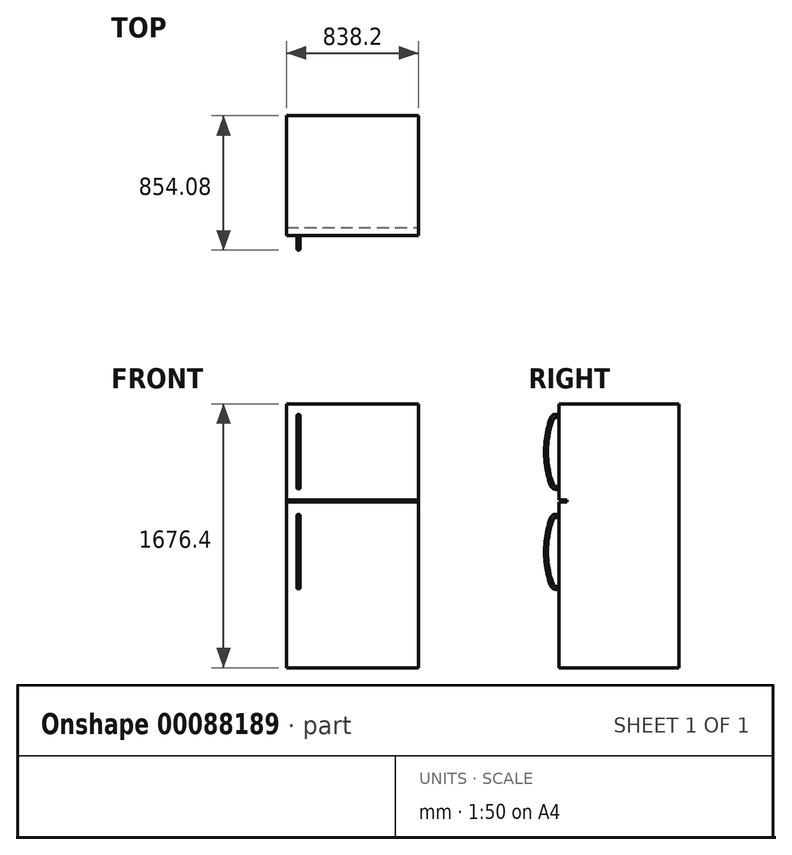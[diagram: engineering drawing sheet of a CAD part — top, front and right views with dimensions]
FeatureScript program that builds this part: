
annotation { "Feature Type Name" : "Feature", "Feature Type Description" : "" }
export const myFeature = defineFeature(function(context is Context, id is Id, definition is map)
    precondition{}
    {
        {
            var Q0;
            Q0=qCreatedBy(makeId("Front.planeOp"),FACE);
            var sketch = newSketch(context, id + "F0", { "sketchPlane" : qUnion([Q0])});
            skLineSegment(sketch, "E0.bottom", {"start": v(0, 0) * mm, "end": v(838.2, 0) * mm});
            skLineSegment(sketch, "E0.top", {"start": v(0, 1676.4) * mm, "end": v(838.2, 1676.4) * mm});
            skLineSegment(sketch, "E0.left", {"start": v(0, 0) * mm, "end": v(0, 1676.4) * mm});
            skLineSegment(sketch, "E0.right", {"start": v(838.2, 0) * mm, "end": v(838.2, 1676.4) * mm});
            skSolve(sketch);
        }
        {
            var Q0;
            Q0 = qSketchRegion(id + "F0", true);
            extrude(context, id + "F1", {"entities" : qUnion([Q0]), "depth" : 762 * mm});
        }
        {
            var Q0;
            Q0=makeQuery(id+"F1.opExtrude","CAP_FACE",FACE,{"disambiguationData":[OSD([sQuery(id+"F0.wireOp",EDGE,"E0.bottom"),sQuery(id+"F0.wireOp",EDGE,"E0.top"),sQuery(id+"F0.wireOp",EDGE,"E0.left"),sQuery(id+"F0.wireOp",EDGE,"E0.right")])],"isStart":false});
            var sketch = newSketch(context, id + "F2", { "sketchPlane" : qUnion([Q0])});
            skLineSegment(sketch, "E1.bottom", {"start": v(0, 1066.8) * mm, "end": v(838.2, 1066.8) * mm});
            skLineSegment(sketch, "E1.top", {"start": v(0, 1054.1) * mm, "end": v(838.2, 1054.1) * mm});
            skLineSegment(sketch, "E1.left", {"start": v(0, 1066.8) * mm, "end": v(0, 1054.1) * mm});
            skLineSegment(sketch, "E1.right", {"start": v(838.2, 1066.8) * mm, "end": v(838.2, 1054.1) * mm});
            skSolve(sketch);
        }
        {
            var Q0;
            Q0 = qSketchRegion(id + "F2", true);
            extrude(context, id + "F3", {"entities" : qUnion([Q0]), "operationType" : NewBodyOperationType.REMOVE, "oppositeDirection" : true, "depth" : 50.8 * mm});
        }
        {
            var Q0;
            Q0=makeQuery(id+"F1.opExtrude","SWEPT_FACE",FACE,{"disambiguationData":[OSD([sQuery(id+"F0.wireOp",EDGE,"E0.left")])]});
            cPlane(context, id + "F4", {"entities" : qUnion([Q0]), "cplaneType" : CPlaneType.OFFSET, "offset" : 76.2 * mm, "oppositeDirection" : true, "width" : 152.4 * mm, "height" : 152.4 * mm});
        }
        {
            var Q0;
            {var subQ0=sQuery(id+"F0.wireOp",EDGE,"E0.top");var subQ1=sQuery(id+"F0.wireOp",EDGE,"E0.left");var subQ2=sQuery(id+"F0.wireOp",EDGE,"E0.right");Q0=makeQuery(id+"F3.boolean.opBoolean","SPLIT",FACE,{"disambiguationData":[TD([makeQuery(id+"F1.opExtrude","SWEPT_FACE",FACE,{"disambiguationData":[OSD([subQ0])]})])],"derivedFrom":makeQuery(id+"F1.opExtrude","CAP_FACE",FACE,{"disambiguationData":[OSD([sQuery(id+"F0.wireOp",EDGE,"E0.bottom"),subQ0,subQ1,subQ2])],"isStart":false})});}
            var sketch = newSketch(context, id + "F5", { "sketchPlane" : qUnion([Q0])});
            skCircle(sketch, "E2", {"center": v(76.2, 1600.2) * mm, "radius": 9.53 * mm});
            skSolve(sketch);
        }
        {
            var Q0;
            Q0=qCreatedBy(id+"F4.planeOp",FACE);
            var sketch = newSketch(context, id + "F6", { "sketchPlane" : qUnion([Q0])});
            skLineSegment(sketch, "E3", {"start": v(762, 1600.2) * mm, "end": v(782.7, 1600.2) * mm});
            skArc(sketch, "E4", {"start": v(806.52, 1159.57) * mm, "mid": v(844.55, 1371.6) * mm, "end": v(806.52, 1583.63) * mm});
            skLineSegment(sketch, "E5", {"start": v(782.7, 1143) * mm, "end": v(762, 1143) * mm});
            skPoint(sketch, "E6.visualSharp", {"position": v(800.1, 1143) * mm});
            skArc(sketch, "E6.filletArc", {"start": v(782.7, 1143) * mm, "mid": v(797.2, 1147.55) * mm, "end": v(806.52, 1159.57) * mm});
            skPoint(sketch, "E7.visualSharp", {"position": v(800.1, 1600.2) * mm});
            skArc(sketch, "E7.filletArc", {"start": v(806.52, 1583.63) * mm, "mid": v(797.2, 1595.65) * mm, "end": v(782.7, 1600.2) * mm});
            skLineSegment(sketch, "E8", {"start": v(234.5, 1371.6) * mm, "end": v(844.55, 1371.6) * mm, "construction": true});
            skSolve(sketch);
        }
        {
            var Q0;
            Q0=makeQuery(id+"F5.imprint","IMPRINT",FACE,{"disambiguationData":[TD([[makeQuery(id+"F5.imprint","IMPRINT",EDGE,{"derivedFrom":sQuery(id+"F5.wireOp",EDGE,"E2")}),1.0]])]});
            var Q1;
            Q1=sQuery(id+"F6.wireOp",EDGE,"E3");
            var Q2;
            Q2=sQuery(id+"F6.wireOp",EDGE,"E7.filletArc");
            var Q3;
            Q3=sQuery(id+"F6.wireOp",EDGE,"E4");
            var Q4;
            Q4=sQuery(id+"F6.wireOp",EDGE,"E6.filletArc");
            var Q5;
            Q5=sQuery(id+"F6.wireOp",EDGE,"E5");
            sweep(context, id + "F7", {"operationType" : NewBodyOperationType.ADD, "profiles" : qUnion([Q0]), "path" : qUnion([Q1, Q2, Q3, Q4, Q5])});
        }
        {
            var Q0;
            Q0=makeQuery(id+"F7.opSweep","SWEPT_FACE",FACE,{"disambiguationData":[OSD([sQuery(id+"F5.wireOp",EDGE,"E2"),sQuery(id+"F6.wireOp",EDGE,"E5")])]});
            var Q1;
            Q1=makeQuery(id+"F7.opSweep","SWEPT_FACE",FACE,{"disambiguationData":[OSD([sQuery(id+"F5.wireOp",EDGE,"E2"),sQuery(id+"F6.wireOp",EDGE,"E6.filletArc")])]});
            var Q2;
            Q2=makeQuery(id+"F7.opSweep","SWEPT_FACE",FACE,{"disambiguationData":[OSD([sQuery(id+"F5.wireOp",EDGE,"E2"),sQuery(id+"F6.wireOp",EDGE,"E4")])]});
            var Q3;
            Q3=makeQuery(id+"F7.opSweep","SWEPT_FACE",FACE,{"disambiguationData":[OSD([sQuery(id+"F5.wireOp",EDGE,"E2"),sQuery(id+"F6.wireOp",EDGE,"E7.filletArc")])]});
            var Q4;
            Q4=makeQuery(id+"F7.opSweep","SWEPT_FACE",FACE,{"disambiguationData":[OSD([sQuery(id+"F5.wireOp",EDGE,"E2"),sQuery(id+"F6.wireOp",EDGE,"E3")])]});
            var Q5;
            Q5=makeQuery(id+"F3.boolean.opBoolean","COPY",FACE,{"derivedFrom":makeQuery(id+"F3.opExtrude","SWEPT_FACE",FACE,{"disambiguationData":[OSD([sQuery(id+"F2.wireOp",EDGE,"E1.top")])]})});
            mirror(context, id + "F8", {"faces" : qUnion([Q0, Q1, Q2, Q3, Q4]), "mirrorPlane" : qUnion([Q5]), "patternType" : MirrorType.FACE});
        }
    });
